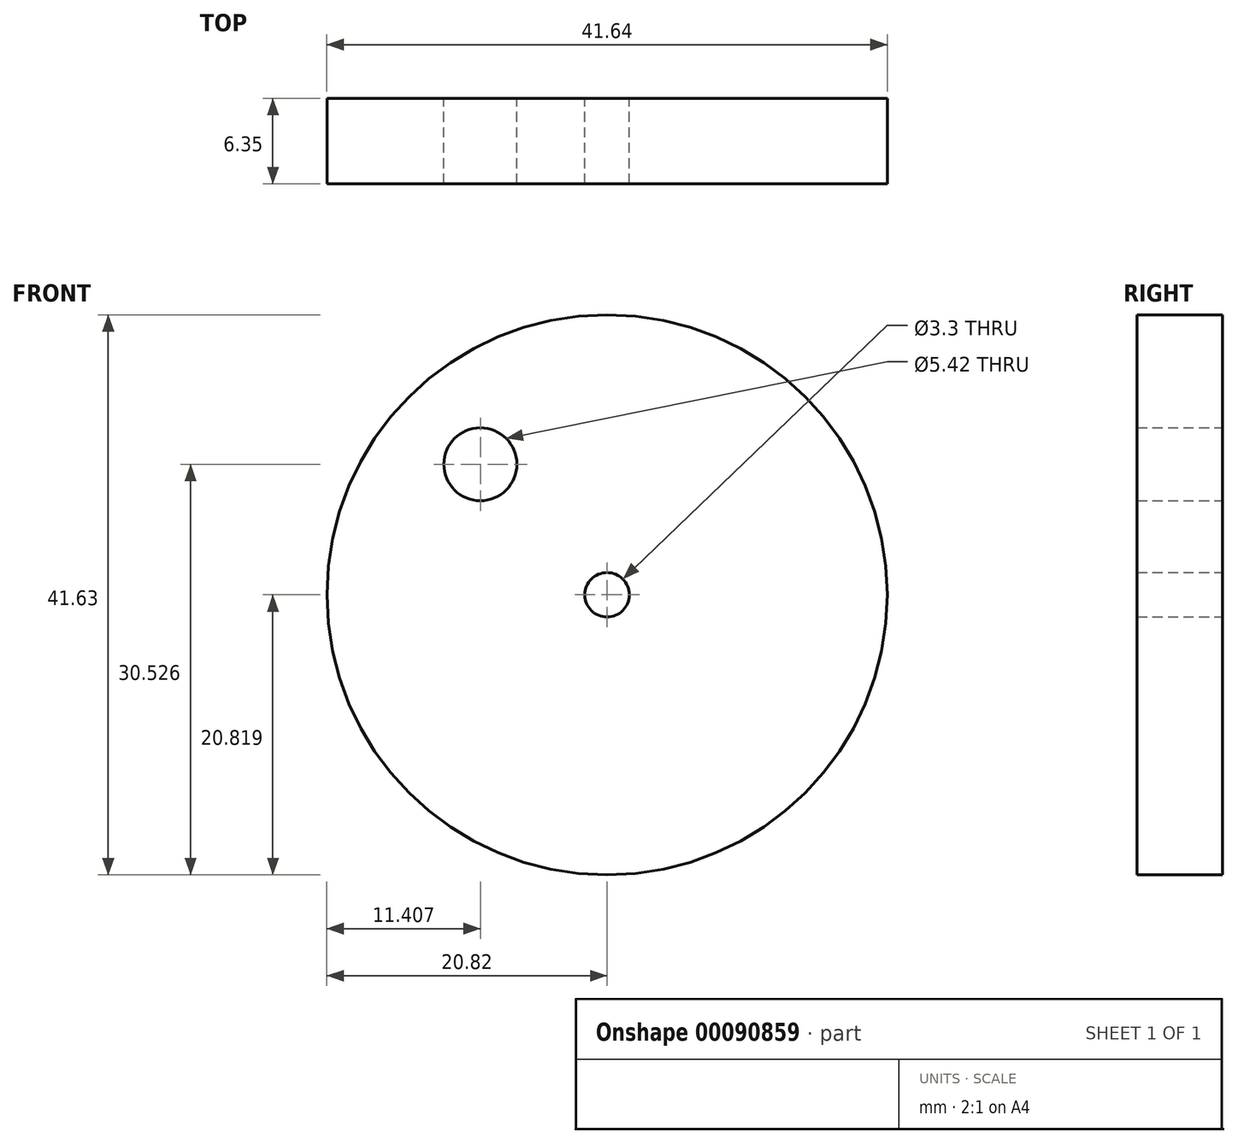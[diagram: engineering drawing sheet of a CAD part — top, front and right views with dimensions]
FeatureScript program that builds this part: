
annotation { "Feature Type Name" : "Feature", "Feature Type Description" : "" }
export const myFeature = defineFeature(function(context is Context, id is Id, definition is map)
    precondition{}
    {
        {
            var Q0;
            Q0=qCreatedBy(makeId("Front.planeOp"),FACE);
            var sketch = newSketch(context, id + "F0", { "sketchPlane" : qUnion([Q0])});
            skCircle(sketch, "E0", {"center": v(-25.15, 21.18) * mm, "radius": 20.82 * mm});
            skCircle(sketch, "E1", {"center": v(-25.15, 21.18) * mm, "radius": 1.65 * mm});
            skCircle(sketch, "E2", {"center": v(-34.56, 30.89) * mm, "radius": 2.71 * mm});
            skSolve(sketch);
        }
        {
            var Q0;
            Q0=makeQuery(id+"F0.imprint","IMPRINT",FACE,{"disambiguationData":[TD([[makeQuery(id+"F0.imprint","IMPRINT",EDGE,{"derivedFrom":sQuery(id+"F0.wireOp",EDGE,"E0")}),1.0]])]});
            extrude(context, id + "F1", {"entities" : qUnion([Q0]), "depth" : 6.35 * mm});
        }
    });
